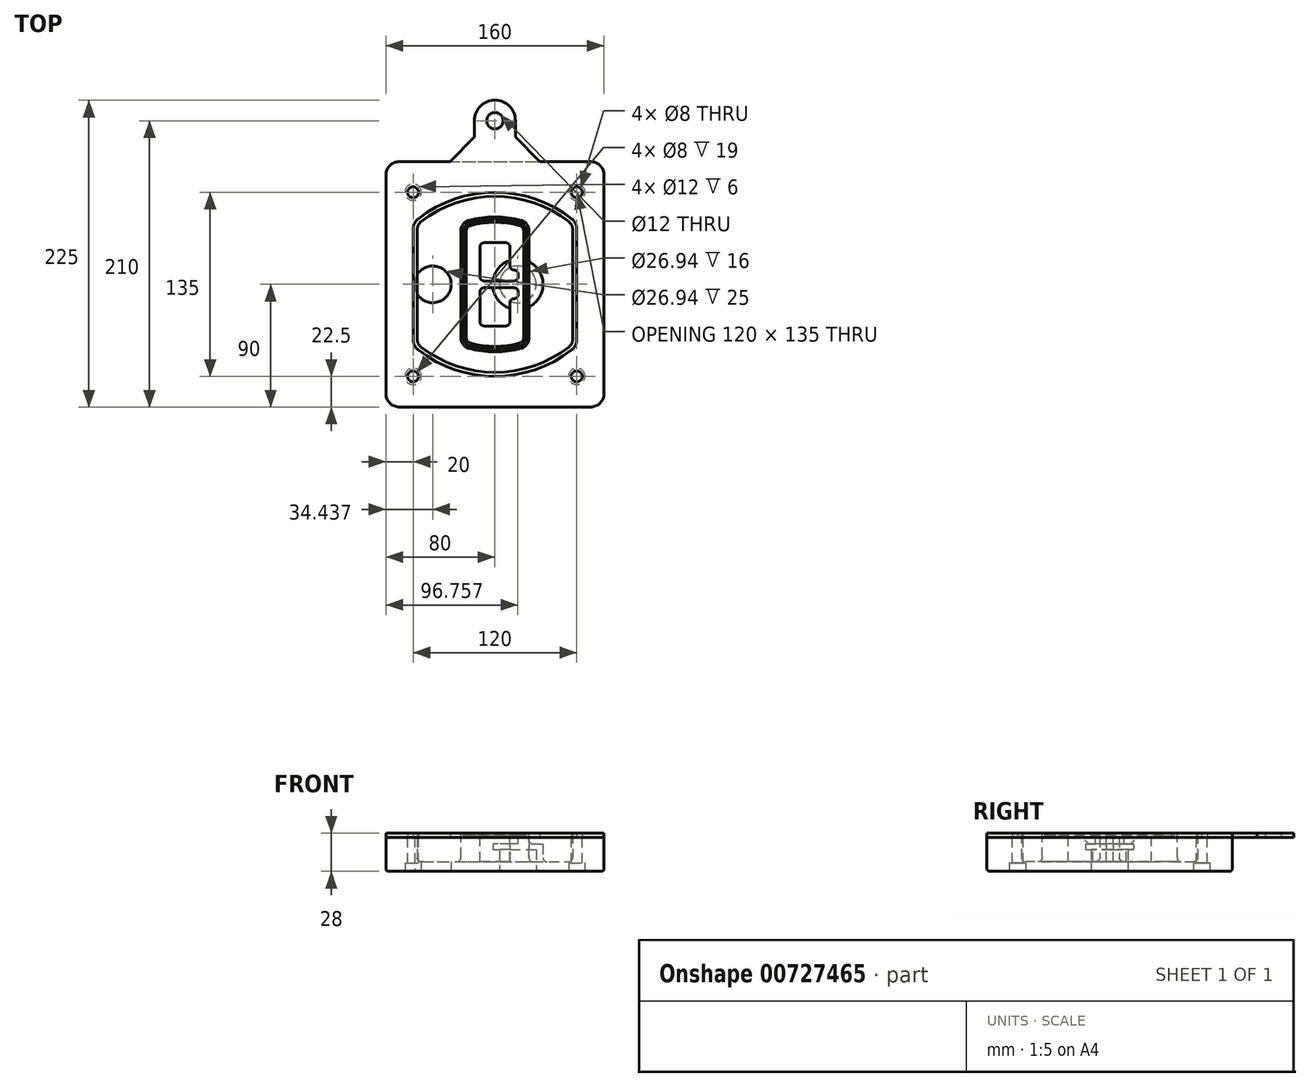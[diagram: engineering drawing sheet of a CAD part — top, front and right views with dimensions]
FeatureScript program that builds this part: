
annotation { "Feature Type Name" : "Feature", "Feature Type Description" : "" }
export const myFeature = defineFeature(function(context is Context, id is Id, definition is map)
    precondition{}
    {
        {
            var Q0;
            Q0=qCreatedBy(makeId("Top.planeOp"),FACE);
            var sketch = newSketch(context, id + "F0", { "sketchPlane" : qUnion([Q0])});
            skPoint(sketch, "E0.rect.middle", {"position": v(0, 0) * mm});
            skLineSegment(sketch, "E1.bottom", {"start": v(-70, -90) * mm, "end": v(70, -90) * mm});
            skLineSegment(sketch, "E1.top", {"start": v(-70, 90) * mm, "end": v(70, 90) * mm});
            skLineSegment(sketch, "E1.left", {"start": v(-80, -80) * mm, "end": v(-80, 80) * mm});
            skLineSegment(sketch, "E1.right", {"start": v(80, -80) * mm, "end": v(80, 80) * mm});
            skLineSegment(sketch, "E2", {"start": v(-80, 90) * mm, "end": v(80, -90) * mm, "construction": true});
            skLineSegment(sketch, "E3", {"start": v(80, 90) * mm, "end": v(-80, -90) * mm, "construction": true});
            skCircle(sketch, "E4", {"center": v(-60, 67.5) * mm, "radius": 4 * mm});
            skCircle(sketch, "E5", {"center": v(60, 67.5) * mm, "radius": 4 * mm});
            skCircle(sketch, "E6", {"center": v(60, -67.5) * mm, "radius": 4 * mm});
            skCircle(sketch, "E7", {"center": v(-60, -67.5) * mm, "radius": 4 * mm});
            skLineSegment(sketch, "E8", {"start": v(-60, 67.5) * mm, "end": v(60, 67.5) * mm, "construction": true});
            skLineSegment(sketch, "E9", {"start": v(60, 67.5) * mm, "end": v(60, -67.5) * mm, "construction": true});
            skLineSegment(sketch, "E10", {"start": v(60, -67.5) * mm, "end": v(-60, -67.5) * mm, "construction": true});
            skLineSegment(sketch, "E11", {"start": v(-60, -67.5) * mm, "end": v(-60, 67.5) * mm, "construction": true});
            skLineSegment(sketch, "E12", {"start": v(-60, 40.3) * mm, "end": v(-60, -40.3) * mm});
            skLineSegment(sketch, "E13", {"start": v(60, 40.3) * mm, "end": v(60, -40.3) * mm});
            skArc(sketch, "E14", {"start": v(56.15, 48.18) * mm, "mid": v(0, 67.5) * mm, "end": v(-56.15, 48.18) * mm});
            skArc(sketch, "E15", {"start": v(-56.15, -48.18) * mm, "mid": v(0, -67.5) * mm, "end": v(56.15, -48.18) * mm});
            skLineSegment(sketch, "E16", {"start": v(-60, 0) * mm, "end": v(60, 0) * mm, "construction": true});
            skPoint(sketch, "E17.visualSharp", {"position": v(-60, -45) * mm});
            skArc(sketch, "E17.filletArc", {"start": v(-60, -40.3) * mm, "mid": v(-58.99, -44.68) * mm, "end": v(-56.15, -48.18) * mm});
            skPoint(sketch, "E18.visualSharp", {"position": v(-60, 45) * mm});
            skArc(sketch, "E18.filletArc", {"start": v(-56.15, 48.18) * mm, "mid": v(-58.99, 44.68) * mm, "end": v(-60, 40.3) * mm});
            skPoint(sketch, "E19.visualSharp", {"position": v(60, 45) * mm});
            skArc(sketch, "E19.filletArc", {"start": v(60, 40.3) * mm, "mid": v(58.99, 44.68) * mm, "end": v(56.15, 48.18) * mm});
            skPoint(sketch, "E20.visualSharp", {"position": v(60, -45) * mm});
            skArc(sketch, "E20.filletArc", {"start": v(56.15, -48.18) * mm, "mid": v(58.99, -44.68) * mm, "end": v(60, -40.3) * mm});
            skPoint(sketch, "E21.visualSharp", {"position": v(-80, 90) * mm});
            skArc(sketch, "E21.filletArc", {"start": v(-70, 90) * mm, "mid": v(-77.07, 87.07) * mm, "end": v(-80, 80) * mm});
            skPoint(sketch, "E22.visualSharp", {"position": v(80, 90) * mm});
            skArc(sketch, "E22.filletArc", {"start": v(80, 80) * mm, "mid": v(77.07, 87.07) * mm, "end": v(70, 90) * mm});
            skPoint(sketch, "E23.visualSharp", {"position": v(80, -90) * mm});
            skArc(sketch, "E23.filletArc", {"start": v(70, -90) * mm, "mid": v(77.07, -87.07) * mm, "end": v(80, -80) * mm});
            skPoint(sketch, "E24.visualSharp", {"position": v(-80, -90) * mm});
            skArc(sketch, "E24.filletArc", {"start": v(-80, -80) * mm, "mid": v(-77.07, -87.07) * mm, "end": v(-70, -90) * mm});
            skArc(sketch, "E25.0", {"start": v(57, 40.3) * mm, "mid": v(56.3, 43.36) * mm, "end": v(54.3, 45.81) * mm});
            skLineSegment(sketch, "E25.1", {"start": v(57, 40.3) * mm, "end": v(57, -40.3) * mm});
            skArc(sketch, "E25.2", {"start": v(54.3, -45.81) * mm, "mid": v(56.3, -43.36) * mm, "end": v(57, -40.3) * mm});
            skArc(sketch, "E25.3", {"start": v(-54.3, -45.81) * mm, "mid": v(0, -64.5) * mm, "end": v(54.3, -45.81) * mm});
            skArc(sketch, "E25.4", {"start": v(-57, -40.3) * mm, "mid": v(-56.3, -43.36) * mm, "end": v(-54.3, -45.81) * mm});
            skArc(sketch, "E25.5", {"start": v(54.3, 45.81) * mm, "mid": v(0, 64.5) * mm, "end": v(-54.3, 45.81) * mm});
            skLineSegment(sketch, "E25.6", {"start": v(-57, 40.3) * mm, "end": v(-57, -40.3) * mm});
            skArc(sketch, "E25.7", {"start": v(-54.3, 45.81) * mm, "mid": v(-56.3, 43.36) * mm, "end": v(-57, 40.3) * mm});
            skArc(sketch, "E26.0", {"start": v(-58.62, 51.33) * mm, "mid": v(-62.58, 46.43) * mm, "end": v(-64, 40.3) * mm});
            skArc(sketch, "E26.1", {"start": v(58.62, 51.33) * mm, "mid": v(0, 71.5) * mm, "end": v(-58.62, 51.33) * mm});
            skArc(sketch, "E26.2", {"start": v(64, 40.3) * mm, "mid": v(62.58, 46.43) * mm, "end": v(58.62, 51.33) * mm});
            skLineSegment(sketch, "E26.3", {"start": v(64, 40.3) * mm, "end": v(64, -40.3) * mm});
            skArc(sketch, "E26.4", {"start": v(58.62, -51.33) * mm, "mid": v(62.58, -46.43) * mm, "end": v(64, -40.3) * mm});
            skLineSegment(sketch, "E26.5", {"start": v(-64, 40.3) * mm, "end": v(-64, -40.3) * mm});
            skArc(sketch, "E26.6", {"start": v(-58.62, -51.33) * mm, "mid": v(0, -71.5) * mm, "end": v(58.62, -51.33) * mm});
            skArc(sketch, "E26.7", {"start": v(-64, -40.3) * mm, "mid": v(-62.58, -46.43) * mm, "end": v(-58.62, -51.33) * mm});
            skSolve(sketch);
        }
        {
            var Q0;
            Q0=makeQuery(id+"F0.imprint","IMPRINT",FACE,{"disambiguationData":[TD([[makeQuery(id+"F0.imprint","IMPRINT",EDGE,{"derivedFrom":sQuery(id+"F0.wireOp",EDGE,"E1.bottom")}),1.0]])]});
            var Q1;
            Q1=makeQuery(id+"F0.imprint","IMPRINT",FACE,{"disambiguationData":[TD([[makeQuery(id+"F0.imprint","IMPRINT",EDGE,{"derivedFrom":sQuery(id+"F0.wireOp",EDGE,"E12")}),1.0]])]});
            var Q2;
            Q2=makeQuery(id+"F0.imprint","IMPRINT",FACE,{"disambiguationData":[TD([[makeQuery(id+"F0.imprint","IMPRINT",EDGE,{"derivedFrom":sQuery(id+"F0.wireOp",EDGE,"E25.0")}),1.0]])]});
            var Q3;
            Q3=makeQuery(id+"F0.imprint","IMPRINT",FACE,{"disambiguationData":[TD([[makeQuery(id+"F0.imprint","IMPRINT",EDGE,{"derivedFrom":sQuery(id+"F0.wireOp",EDGE,"E12")}),-1.0]])]});
            extrude(context, id + "F1", {"entities" : qUnion([Q0, Q1, Q2, Q3]), "oppositeDirection" : true, "depth" : 25 * mm});
        }
        {
            var Q0;
            Q0=makeQuery(id+"F0.imprint","IMPRINT",FACE,{"disambiguationData":[TD([[makeQuery(id+"F0.imprint","IMPRINT",EDGE,{"derivedFrom":sQuery(id+"F0.wireOp",EDGE,"E12")}),1.0]])]});
            extrude(context, id + "F2", {"entities" : qUnion([Q0]), "operationType" : NewBodyOperationType.ADD, "depth" : 3 * mm});
        }
        {
            var Q0;
            Q0=makeQuery(id+"F0.imprint","IMPRINT",FACE,{"disambiguationData":[TD([[makeQuery(id+"F0.imprint","IMPRINT",EDGE,{"derivedFrom":sQuery(id+"F0.wireOp",EDGE,"E25.0")}),1.0]])]});
            extrude(context, id + "F3", {"entities" : qUnion([Q0]), "operationType" : NewBodyOperationType.REMOVE, "oppositeDirection" : true, "depth" : 18 * mm});
        }
        {
            var Q0;
            Q0=makeQuery(id+"F2.opExtrude","CAP_FACE",FACE,{"disambiguationData":[OSD([sQuery(id+"F0.wireOp",EDGE,"E12"),sQuery(id+"F0.wireOp",EDGE,"E13"),sQuery(id+"F0.wireOp",EDGE,"E14"),sQuery(id+"F0.wireOp",EDGE,"E15"),sQuery(id+"F0.wireOp",EDGE,"E17.filletArc"),sQuery(id+"F0.wireOp",EDGE,"E18.filletArc"),sQuery(id+"F0.wireOp",EDGE,"E19.filletArc"),sQuery(id+"F0.wireOp",EDGE,"E20.filletArc"),sQuery(id+"F0.wireOp",EDGE,"E25.0"),sQuery(id+"F0.wireOp",EDGE,"E25.1"),sQuery(id+"F0.wireOp",EDGE,"E25.2"),sQuery(id+"F0.wireOp",EDGE,"E25.3"),sQuery(id+"F0.wireOp",EDGE,"E25.4"),sQuery(id+"F0.wireOp",EDGE,"E25.5"),sQuery(id+"F0.wireOp",EDGE,"E25.6"),sQuery(id+"F0.wireOp",EDGE,"E25.7")])],"isStart":false});
            var sketch = newSketch(context, id + "F4", { "sketchPlane" : qUnion([Q0])});
            skArc(sketch, "E27.0", {"start": v(-19.08, -46.97) * mm, "mid": v(0, -49.5) * mm, "end": v(19.08, -46.97) * mm});
            skArc(sketch, "E28.0", {"start": v(19.08, 46.97) * mm, "mid": v(0, 49.5) * mm, "end": v(-19.08, 46.97) * mm});
            skLineSegment(sketch, "E29", {"start": v(-25, 39.25) * mm, "end": v(-25, -39.25) * mm});
            skLineSegment(sketch, "E30", {"start": v(25, 39.25) * mm, "end": v(25, -39.25) * mm});
            skLineSegment(sketch, "E31", {"start": v(-25, 45.1) * mm, "end": v(25, 45.1) * mm, "construction": true});
            skLineSegment(sketch, "E32", {"start": v(-25, -45.1) * mm, "end": v(25, -45.1) * mm, "construction": true});
            skPoint(sketch, "E33.visualSharp", {"position": v(-25, 45.1) * mm});
            skArc(sketch, "E33.filletArc", {"start": v(-19.08, 46.97) * mm, "mid": v(-23.35, 44.11) * mm, "end": v(-25, 39.25) * mm});
            skPoint(sketch, "E34.visualSharp", {"position": v(25, 45.1) * mm});
            skArc(sketch, "E34.filletArc", {"start": v(25, 39.25) * mm, "mid": v(23.35, 44.11) * mm, "end": v(19.08, 46.97) * mm});
            skPoint(sketch, "E35.visualSharp", {"position": v(25, -45.1) * mm});
            skArc(sketch, "E35.filletArc", {"start": v(19.08, -46.97) * mm, "mid": v(23.35, -44.11) * mm, "end": v(25, -39.25) * mm});
            skPoint(sketch, "E36.visualSharp", {"position": v(-25, -45.1) * mm});
            skArc(sketch, "E36.filletArc", {"start": v(-25, -39.25) * mm, "mid": v(-23.35, -44.11) * mm, "end": v(-19.08, -46.97) * mm});
            skArc(sketch, "E37.0", {"start": v(54.3, 45.81) * mm, "mid": v(0, 64.5) * mm, "end": v(-54.3, 45.81) * mm});
            skArc(sketch, "E37.1", {"start": v(-54.3, 45.81) * mm, "mid": v(-56.3, 43.36) * mm, "end": v(-57, 40.3) * mm});
            skLineSegment(sketch, "E37.2", {"start": v(-57, 40.3) * mm, "end": v(-57, -40.3) * mm});
            skArc(sketch, "E37.3", {"start": v(-57, -40.3) * mm, "mid": v(-56.3, -43.36) * mm, "end": v(-54.3, -45.81) * mm});
            skArc(sketch, "E37.4", {"start": v(-54.3, -45.81) * mm, "mid": v(0, -64.5) * mm, "end": v(54.3, -45.81) * mm});
            skArc(sketch, "E37.5", {"start": v(54.3, -45.81) * mm, "mid": v(56.3, -43.36) * mm, "end": v(57, -40.3) * mm});
            skLineSegment(sketch, "E37.6", {"start": v(57, 40.3) * mm, "end": v(57, -40.3) * mm});
            skArc(sketch, "E37.7", {"start": v(57, 40.3) * mm, "mid": v(56.3, 43.36) * mm, "end": v(54.3, 45.81) * mm});
            skLineSegment(sketch, "E38.0", {"start": v(23, 39.25) * mm, "end": v(23, -39.25) * mm});
            skArc(sketch, "E38.1", {"start": v(18.56, -45.04) * mm, "mid": v(21.76, -42.9) * mm, "end": v(23, -39.25) * mm});
            skArc(sketch, "E38.2", {"start": v(-18.56, -45.04) * mm, "mid": v(0, -47.5) * mm, "end": v(18.56, -45.04) * mm});
            skArc(sketch, "E38.3", {"start": v(-23, -39.25) * mm, "mid": v(-21.76, -42.9) * mm, "end": v(-18.56, -45.04) * mm});
            skLineSegment(sketch, "E38.4", {"start": v(-23, 39.25) * mm, "end": v(-23, -39.25) * mm});
            skArc(sketch, "E38.5", {"start": v(23, 39.25) * mm, "mid": v(21.76, 42.9) * mm, "end": v(18.56, 45.04) * mm});
            skArc(sketch, "E38.6", {"start": v(-18.56, 45.04) * mm, "mid": v(-21.76, 42.9) * mm, "end": v(-23, 39.25) * mm});
            skArc(sketch, "E38.7", {"start": v(18.56, 45.04) * mm, "mid": v(0, 47.5) * mm, "end": v(-18.56, 45.04) * mm});
            skArc(sketch, "E39.0", {"start": v(21, 39.25) * mm, "mid": v(20.18, 41.68) * mm, "end": v(18.04, 43.1) * mm});
            skLineSegment(sketch, "E39.1", {"start": v(21, 39.25) * mm, "end": v(21, -39.25) * mm});
            skArc(sketch, "E39.2", {"start": v(18.04, -43.1) * mm, "mid": v(20.18, -41.68) * mm, "end": v(21, -39.25) * mm});
            skArc(sketch, "E39.3", {"start": v(-18.04, -43.1) * mm, "mid": v(0, -45.5) * mm, "end": v(18.04, -43.1) * mm});
            skArc(sketch, "E39.4", {"start": v(-21, -39.25) * mm, "mid": v(-20.18, -41.68) * mm, "end": v(-18.04, -43.1) * mm});
            skArc(sketch, "E39.5", {"start": v(18.04, 43.1) * mm, "mid": v(0, 45.5) * mm, "end": v(-18.04, 43.1) * mm});
            skLineSegment(sketch, "E39.6", {"start": v(-21, 39.25) * mm, "end": v(-21, -39.25) * mm});
            skArc(sketch, "E39.7", {"start": v(-18.04, 43.1) * mm, "mid": v(-20.18, 41.68) * mm, "end": v(-21, 39.25) * mm});
            skLineSegment(sketch, "E40", {"start": v(-25, 0) * mm, "end": v(25, 0) * mm, "construction": true});
            skLineSegment(sketch, "E41", {"start": v(-11, 5.5) * mm, "end": v(-11, 27.5) * mm});
            skLineSegment(sketch, "E42", {"start": v(-8, 30.5) * mm, "end": v(8, 30.5) * mm});
            skLineSegment(sketch, "E43", {"start": v(11, 27.5) * mm, "end": v(11, 13.5) * mm});
            skLineSegment(sketch, "E44", {"start": v(14, 10.5) * mm, "end": v(14, 10.5) * mm});
            skLineSegment(sketch, "E45", {"start": v(17, 7.5) * mm, "end": v(17, 5.5) * mm});
            skLineSegment(sketch, "E46", {"start": v(14, 2.5) * mm, "end": v(-8, 2.5) * mm});
            skPoint(sketch, "E47.visualSharp", {"position": v(-11, 30.5) * mm});
            skArc(sketch, "E47.filletArc", {"start": v(-8, 30.5) * mm, "mid": v(-10.12, 29.62) * mm, "end": v(-11, 27.5) * mm});
            skPoint(sketch, "E48.visualSharp", {"position": v(11, 30.5) * mm});
            skArc(sketch, "E48.filletArc", {"start": v(11, 27.5) * mm, "mid": v(10.12, 29.62) * mm, "end": v(8, 30.5) * mm});
            skPoint(sketch, "E49.visualSharp", {"position": v(11, 10.5) * mm});
            skArc(sketch, "E49.filletArc", {"start": v(11, 13.5) * mm, "mid": v(11.88, 11.38) * mm, "end": v(14, 10.5) * mm});
            skPoint(sketch, "E50.visualSharp", {"position": v(17, 10.5) * mm});
            skArc(sketch, "E50.filletArc", {"start": v(17, 7.5) * mm, "mid": v(16.12, 9.62) * mm, "end": v(14, 10.5) * mm});
            skPoint(sketch, "E51.visualSharp", {"position": v(17, 2.5) * mm});
            skArc(sketch, "E51.filletArc", {"start": v(14, 2.5) * mm, "mid": v(16.12, 3.38) * mm, "end": v(17, 5.5) * mm});
            skPoint(sketch, "E52.visualSharp", {"position": v(-11, 2.5) * mm});
            skArc(sketch, "E52.filletArc", {"start": v(-11, 5.5) * mm, "mid": v(-10.12, 3.38) * mm, "end": v(-8, 2.5) * mm});
            skLineSegment(sketch, "E53.0.MirrorCS", {"start": v(14, -2.5) * mm, "end": v(-8, -2.5) * mm});
            skArc(sketch, "E54.0.MirrorCS", {"start": v(-11, -5.5) * mm, "mid": v(-10.12, -3.38) * mm, "end": v(-8, -2.5) * mm});
            skLineSegment(sketch, "E55.0.MirrorCS", {"start": v(-11, -5.5) * mm, "end": v(-11, -27.5) * mm});
            skArc(sketch, "E56.0.MirrorCS", {"start": v(-8, -30.5) * mm, "mid": v(-10.12, -29.62) * mm, "end": v(-11, -27.5) * mm});
            skLineSegment(sketch, "E57.0.MirrorCS", {"start": v(-8, -30.5) * mm, "end": v(8, -30.5) * mm});
            skArc(sketch, "E58.0.MirrorCS", {"start": v(11, -27.5) * mm, "mid": v(10.12, -29.62) * mm, "end": v(8, -30.5) * mm});
            skLineSegment(sketch, "E59.0.MirrorCS", {"start": v(11, -27.5) * mm, "end": v(11, -13.5) * mm});
            skArc(sketch, "E60.0.MirrorCS", {"start": v(11, -13.5) * mm, "mid": v(11.88, -11.38) * mm, "end": v(14, -10.5) * mm});
            skArc(sketch, "E61.0.MirrorCS", {"start": v(17, -7.5) * mm, "mid": v(16.12, -9.62) * mm, "end": v(14, -10.5) * mm});
            skLineSegment(sketch, "E62.0.MirrorCS", {"start": v(17, -7.5) * mm, "end": v(17, -5.5) * mm});
            skArc(sketch, "E63.0.MirrorCS", {"start": v(14, -2.5) * mm, "mid": v(16.12, -3.38) * mm, "end": v(17, -5.5) * mm});
            skSolve(sketch);
        }
        {
            var Q0;
            Q0=makeQuery(id+"F4.imprint","IMPRINT",FACE,{"disambiguationData":[TD([[makeQuery(id+"F4.imprint","IMPRINT",EDGE,{"derivedFrom":sQuery(id+"F4.wireOp",EDGE,"E27.0")}),1.0]])]});
            var Q1;
            Q1=makeQuery(id+"F4.imprint","IMPRINT",FACE,{"disambiguationData":[TD([[makeQuery(id+"F4.imprint","IMPRINT",EDGE,{"derivedFrom":sQuery(id+"F4.wireOp",EDGE,"E38.0")}),-1.0]])]});
            var Q2;
            Q2=makeQuery(id+"F4.imprint","IMPRINT",FACE,{"disambiguationData":[TD([[makeQuery(id+"F4.imprint","IMPRINT",EDGE,{"derivedFrom":sQuery(id+"F4.wireOp",EDGE,"E39.0")}),1.0]])]});
            extrude(context, id + "F5", {"entities" : qUnion([Q0, Q1, Q2]), "operationType" : NewBodyOperationType.ADD, "endBound" : BoundingType.UP_TO_NEXT, "oppositeDirection" : true, "depth" : 25 * mm});
        }
        {
            var Q0;
            Q0=makeQuery(id+"F4.imprint","IMPRINT",FACE,{"disambiguationData":[TD([[makeQuery(id+"F4.imprint","IMPRINT",EDGE,{"derivedFrom":sQuery(id+"F4.wireOp",EDGE,"E38.0")}),-1.0]])]});
            extrude(context, id + "F6", {"entities" : qUnion([Q0]), "operationType" : NewBodyOperationType.REMOVE, "oppositeDirection" : true, "depth" : 2 * mm});
        }
        {
            var Q0;
            Q0=makeQuery(id+"F1.opExtrude","CAP_FACE",FACE,{"disambiguationData":[OSD([sQuery(id+"F0.wireOp",EDGE,"E1.bottom"),sQuery(id+"F0.wireOp",EDGE,"E1.top"),sQuery(id+"F0.wireOp",EDGE,"E1.left"),sQuery(id+"F0.wireOp",EDGE,"E1.right"),sQuery(id+"F0.wireOp",EDGE,"E4"),sQuery(id+"F0.wireOp",EDGE,"E5"),sQuery(id+"F0.wireOp",EDGE,"E6"),sQuery(id+"F0.wireOp",EDGE,"E7"),sQuery(id+"F0.wireOp",EDGE,"E21.filletArc"),sQuery(id+"F0.wireOp",EDGE,"E22.filletArc"),sQuery(id+"F0.wireOp",EDGE,"E23.filletArc"),sQuery(id+"F0.wireOp",EDGE,"E24.filletArc")])],"isStart":false});
            var sketch = newSketch(context, id + "F7", { "sketchPlane" : qUnion([Q0])});
            skCircle(sketch, "E64", {"center": v(16.76, 0) * mm, "radius": 13.47 * mm});
            skCircle(sketch, "E65", {"center": v(-45.56, 0) * mm, "radius": 13.47 * mm});
            skLineSegment(sketch, "E66", {"start": v(80, 0) * mm, "end": v(-80, 0) * mm});
            skCircle(sketch, "E67", {"center": v(16.76, 0) * mm, "radius": 18.47 * mm});
            skCircle(sketch, "E68", {"center": v(60, -67.5) * mm, "radius": 6 * mm});
            skCircle(sketch, "E69", {"center": v(-60, -67.5) * mm, "radius": 6 * mm});
            skCircle(sketch, "E70", {"center": v(-60, 67.5) * mm, "radius": 6 * mm});
            skCircle(sketch, "E71", {"center": v(60, 67.5) * mm, "radius": 6 * mm});
            skSolve(sketch);
        }
        {
            var Q0;
            {var subQ1=sQuery(id+"F7.wireOp",EDGE,"E66");var subQ4=sQuery(id+"F7.wireOp",EDGE,"E64");var subQ6=makeQuery(id+"F7.imprint","INTERSECT",VERTEX,{"disambiguationData":[OD(0.0)],"derivedFrom":[subQ4,subQ1]});Q0=makeQuery(id+"F7.imprint","IMPRINT",FACE,{"disambiguationData":[TD([[makeQuery(id+"F7.imprint","IMPRINT",EDGE,{"disambiguationData":[TD([[subQ6,-1.0]])],"derivedFrom":subQ4}),-1.0]])]});}
            var Q1;
            {var subQ0=sQuery(id+"F7.wireOp",EDGE,"E66");var subQ1=sQuery(id+"F7.wireOp",EDGE,"E64");var subQ3=makeQuery(id+"F7.imprint","INTERSECT",VERTEX,{"disambiguationData":[OD(0.0)],"derivedFrom":[subQ1,subQ0]});Q1=makeQuery(id+"F7.imprint","IMPRINT",FACE,{"disambiguationData":[TD([[makeQuery(id+"F7.imprint","IMPRINT",EDGE,{"disambiguationData":[TD([[subQ3,-1.0]])],"derivedFrom":subQ1}),1.0]])]});}
            var Q2;
            {var subQ0=sQuery(id+"F7.wireOp",EDGE,"E66");var subQ1=sQuery(id+"F7.wireOp",EDGE,"E64");var subQ3=makeQuery(id+"F7.imprint","INTERSECT",VERTEX,{"disambiguationData":[OD(0.0)],"derivedFrom":[subQ1,subQ0]});Q2=makeQuery(id+"F7.imprint","IMPRINT",FACE,{"disambiguationData":[TD([[makeQuery(id+"F7.imprint","IMPRINT",EDGE,{"disambiguationData":[TD([[subQ3,1.0]])],"derivedFrom":subQ1}),1.0]])]});}
            var Q3;
            {var subQ1=sQuery(id+"F7.wireOp",EDGE,"E66");var subQ4=sQuery(id+"F7.wireOp",EDGE,"E64");var subQ6=makeQuery(id+"F7.imprint","INTERSECT",VERTEX,{"disambiguationData":[OD(0.0)],"derivedFrom":[subQ4,subQ1]});Q3=makeQuery(id+"F7.imprint","IMPRINT",FACE,{"disambiguationData":[TD([[makeQuery(id+"F7.imprint","IMPRINT",EDGE,{"disambiguationData":[TD([[subQ6,1.0]])],"derivedFrom":subQ4}),-1.0]])]});}
            extrude(context, id + "F8", {"entities" : qUnion([Q0, Q1, Q2, Q3]), "operationType" : NewBodyOperationType.ADD, "oppositeDirection" : true, "depth" : 20 * mm});
        }
        {
            var Q0;
            {var subQ0=sQuery(id+"F7.wireOp",EDGE,"E66");var subQ1=sQuery(id+"F7.wireOp",EDGE,"E64");var subQ3=makeQuery(id+"F7.imprint","INTERSECT",VERTEX,{"disambiguationData":[OD(0.0)],"derivedFrom":[subQ1,subQ0]});Q0=makeQuery(id+"F7.imprint","IMPRINT",FACE,{"disambiguationData":[TD([[makeQuery(id+"F7.imprint","IMPRINT",EDGE,{"disambiguationData":[TD([[subQ3,-1.0]])],"derivedFrom":subQ1}),1.0]])]});}
            var Q1;
            {var subQ0=sQuery(id+"F7.wireOp",EDGE,"E66");var subQ1=sQuery(id+"F7.wireOp",EDGE,"E64");var subQ3=makeQuery(id+"F7.imprint","INTERSECT",VERTEX,{"disambiguationData":[OD(0.0)],"derivedFrom":[subQ1,subQ0]});Q1=makeQuery(id+"F7.imprint","IMPRINT",FACE,{"disambiguationData":[TD([[makeQuery(id+"F7.imprint","IMPRINT",EDGE,{"disambiguationData":[TD([[subQ3,1.0]])],"derivedFrom":subQ1}),1.0]])]});}
            extrude(context, id + "F9", {"entities" : qUnion([Q0, Q1]), "operationType" : NewBodyOperationType.REMOVE, "oppositeDirection" : true, "depth" : 16 * mm});
        }
        {
            var Q0;
            {var subQ0=sQuery(id+"F7.wireOp",EDGE,"E66");var subQ1=sQuery(id+"F7.wireOp",EDGE,"E65");var subQ3=makeQuery(id+"F7.imprint","INTERSECT",VERTEX,{"disambiguationData":[OD(0.0)],"derivedFrom":[subQ1,subQ0]});Q0=makeQuery(id+"F7.imprint","IMPRINT",FACE,{"disambiguationData":[TD([[makeQuery(id+"F7.imprint","IMPRINT",EDGE,{"disambiguationData":[TD([[subQ3,-1.0]])],"derivedFrom":subQ1}),1.0]])]});}
            var Q1;
            {var subQ0=sQuery(id+"F7.wireOp",EDGE,"E66");var subQ1=sQuery(id+"F7.wireOp",EDGE,"E65");var subQ3=makeQuery(id+"F7.imprint","INTERSECT",VERTEX,{"disambiguationData":[OD(0.0)],"derivedFrom":[subQ1,subQ0]});Q1=makeQuery(id+"F7.imprint","IMPRINT",FACE,{"disambiguationData":[TD([[makeQuery(id+"F7.imprint","IMPRINT",EDGE,{"disambiguationData":[TD([[subQ3,1.0]])],"derivedFrom":subQ1}),1.0]])]});}
            extrude(context, id + "F10", {"entities" : qUnion([Q0, Q1]), "operationType" : NewBodyOperationType.REMOVE, "oppositeDirection" : true, "depth" : 25 * mm});
        }
        {
            var Q0;
            Q0=makeQuery(id+"F7.imprint","IMPRINT",FACE,{"disambiguationData":[TD([[makeQuery(id+"F7.imprint","IMPRINT",EDGE,{"derivedFrom":sQuery(id+"F7.wireOp",EDGE,"E68")}),1.0]])]});
            var Q1;
            Q1=makeQuery(id+"F7.imprint","IMPRINT",FACE,{"disambiguationData":[TD([[makeQuery(id+"F7.imprint","IMPRINT",EDGE,{"derivedFrom":makeQuery(id+"F1.opExtrude","CAP_EDGE",EDGE,{"disambiguationData":[OSD([sQuery(id+"F0.wireOp",EDGE,"E5")])],"isStart":false})}),-1.0]])]});
            var Q2;
            Q2=makeQuery(id+"F7.imprint","IMPRINT",FACE,{"disambiguationData":[TD([[makeQuery(id+"F7.imprint","IMPRINT",EDGE,{"derivedFrom":sQuery(id+"F7.wireOp",EDGE,"E69")}),1.0]])]});
            var Q3;
            Q3=makeQuery(id+"F7.imprint","IMPRINT",FACE,{"disambiguationData":[TD([[makeQuery(id+"F7.imprint","IMPRINT",EDGE,{"derivedFrom":makeQuery(id+"F1.opExtrude","CAP_EDGE",EDGE,{"disambiguationData":[OSD([sQuery(id+"F0.wireOp",EDGE,"E4")])],"isStart":false})}),-1.0]])]});
            var Q4;
            Q4=makeQuery(id+"F7.imprint","IMPRINT",FACE,{"disambiguationData":[TD([[makeQuery(id+"F7.imprint","IMPRINT",EDGE,{"derivedFrom":sQuery(id+"F7.wireOp",EDGE,"E70")}),1.0]])]});
            var Q5;
            Q5=makeQuery(id+"F7.imprint","IMPRINT",FACE,{"disambiguationData":[TD([[makeQuery(id+"F7.imprint","IMPRINT",EDGE,{"derivedFrom":makeQuery(id+"F1.opExtrude","CAP_EDGE",EDGE,{"disambiguationData":[OSD([sQuery(id+"F0.wireOp",EDGE,"E7")])],"isStart":false})}),-1.0]])]});
            var Q6;
            Q6=makeQuery(id+"F7.imprint","IMPRINT",FACE,{"disambiguationData":[TD([[makeQuery(id+"F7.imprint","IMPRINT",EDGE,{"derivedFrom":sQuery(id+"F7.wireOp",EDGE,"E71")}),1.0]])]});
            var Q7;
            Q7=makeQuery(id+"F7.imprint","IMPRINT",FACE,{"disambiguationData":[TD([[makeQuery(id+"F7.imprint","IMPRINT",EDGE,{"derivedFrom":makeQuery(id+"F1.opExtrude","CAP_EDGE",EDGE,{"disambiguationData":[OSD([sQuery(id+"F0.wireOp",EDGE,"E6")])],"isStart":false})}),-1.0]])]});
            extrude(context, id + "F11", {"entities" : qUnion([Q0, Q1, Q2, Q3, Q4, Q5, Q6, Q7]), "operationType" : NewBodyOperationType.REMOVE, "oppositeDirection" : true, "depth" : 6 * mm});
        }
        {
            var Q0;
            Q0=makeQuery(id+"F9.boolean.opBoolean","COPY",FACE,{"derivedFrom":makeQuery(id+"F9.opExtrude","CAP_FACE",FACE,{"disambiguationData":[OSD([sQuery(id+"F7.wireOp",EDGE,"E64")])],"isStart":false})});
            var sketch = newSketch(context, id + "F12", { "sketchPlane" : qUnion([Q0])});
            skArc(sketch, "E72.0", {"start": v(11, 17.55) * mm, "mid": v(2.57, 11.82) * mm, "end": v(-1.54, 2.5) * mm});
            skArc(sketch, "E72.1", {"start": v(-1.54, -2.5) * mm, "mid": v(2.57, -11.82) * mm, "end": v(11, -17.55) * mm});
            skLineSegment(sketch, "E73", {"start": v(-1.54, -2.5) * mm, "end": v(14, -2.5) * mm});
            skLineSegment(sketch, "E74.0", {"start": v(14, 2.5) * mm, "end": v(-1.54, 2.5) * mm});
            skArc(sketch, "E74.1", {"start": v(14, 2.5) * mm, "mid": v(16.12, 3.38) * mm, "end": v(17, 5.5) * mm});
            skLineSegment(sketch, "E74.2", {"start": v(17, 7.5) * mm, "end": v(17, 5.5) * mm});
            skArc(sketch, "E74.3", {"start": v(17, 7.5) * mm, "mid": v(16.12, 9.62) * mm, "end": v(14, 10.5) * mm});
            skArc(sketch, "E74.4", {"start": v(11, 13.5) * mm, "mid": v(11.88, 11.38) * mm, "end": v(14, 10.5) * mm});
            skLineSegment(sketch, "E74.5", {"start": v(11, 17.55) * mm, "end": v(11, 13.5) * mm});
            skLineSegment(sketch, "E74.7", {"start": v(14, -2.5) * mm, "end": v(-1.54, -2.5) * mm});
            skArc(sketch, "E74.8", {"start": v(14, -2.5) * mm, "mid": v(16.12, -3.38) * mm, "end": v(17, -5.5) * mm});
            skLineSegment(sketch, "E74.9", {"start": v(17, -7.5) * mm, "end": v(17, -5.5) * mm});
            skArc(sketch, "E74.10", {"start": v(17, -7.5) * mm, "mid": v(16.12, -9.62) * mm, "end": v(14, -10.5) * mm});
            skArc(sketch, "E74.11", {"start": v(11, -13.5) * mm, "mid": v(11.88, -11.38) * mm, "end": v(14, -10.5) * mm});
            skLineSegment(sketch, "E74.12", {"start": v(11, -17.55) * mm, "end": v(11, -13.5) * mm});
            skPoint(sketch, "E75.orphan", {"position": v(11, -27.5) * mm});
            skPoint(sketch, "E76.orphan", {"position": v(-8, -2.5) * mm});
            skPoint(sketch, "E77.orphan", {"position": v(-8, 2.5) * mm});
            skPoint(sketch, "E78.orphan", {"position": v(11, 27.5) * mm});
            skSolve(sketch);
        }
        {
            var Q0;
            {var subQ7=sQuery(id+"F12.wireOp",EDGE,"E72.0");var subQ14=sQuery(id+"F12.wireOp",EDGE,"E72.1");var subQ16=sQuery(id+"F12.wireOp",EDGE,"E74.1");var subQ18=sQuery(id+"F12.wireOp",EDGE,"E74.8");Q0=qUnion([makeQuery(id+"F12.imprint","IMPRINT",FACE,{"disambiguationData":[TD([[makeQuery(id+"F12.imprint","IMPRINT",EDGE,{"derivedFrom":subQ7}),1.0]])]}),makeQuery(id+"F12.imprint","IMPRINT",FACE,{"disambiguationData":[TD([[makeQuery(id+"F12.imprint","IMPRINT",EDGE,{"derivedFrom":subQ14}),1.0]])]}),makeQuery(id+"F12.imprint","IMPRINT",FACE,{"disambiguationData":[TD([[makeQuery(id+"F12.imprint","IMPRINT",EDGE,{"derivedFrom":subQ16}),1.0]])]}),makeQuery(id+"F12.imprint","IMPRINT",FACE,{"disambiguationData":[TD([[makeQuery(id+"F12.imprint","IMPRINT",EDGE,{"derivedFrom":subQ18}),-1.0]])]})]);}
            var Q1;
            Q1=makeQuery(id+"F5.boolean.opBoolean","SPLIT",FACE,{"disambiguationData":[TD([makeQuery(id+"F5.opExtrude","SWEPT_FACE",FACE,{"disambiguationData":[OSD([sQuery(id+"F4.wireOp",EDGE,"E41")])]})])],"derivedFrom":makeQuery(id+"F3.boolean.opBoolean","COPY",FACE,{"derivedFrom":makeQuery(id+"F3.opExtrude","CAP_FACE",FACE,{"disambiguationData":[OSD([sQuery(id+"F0.wireOp",EDGE,"E25.0"),sQuery(id+"F0.wireOp",EDGE,"E25.1"),sQuery(id+"F0.wireOp",EDGE,"E25.2"),sQuery(id+"F0.wireOp",EDGE,"E25.3"),sQuery(id+"F0.wireOp",EDGE,"E25.4"),sQuery(id+"F0.wireOp",EDGE,"E25.5"),sQuery(id+"F0.wireOp",EDGE,"E25.6"),sQuery(id+"F0.wireOp",EDGE,"E25.7")])],"isStart":false})})});
            extrude(context, id + "F13", {"entities" : qUnion([Q0]), "operationType" : NewBodyOperationType.REMOVE, "endBound" : BoundingType.UP_TO_SURFACE, "endBoundEntityFace" : qUnion([Q1]), "depth" : 25 * mm});
        }
        {
            var Q0;
            Q0=makeQuery(id+"F3.boolean.opBoolean","COPY",EDGE,{"derivedFrom":makeQuery(id+"F3.opExtrude","CAP_EDGE",EDGE,{"disambiguationData":[OSD([sQuery(id+"F0.wireOp",EDGE,"E25.6")])],"isStart":false})});
            var Q1;
            Q1=makeQuery(id+"F8.boolean.opBoolean","INTERSECT",EDGE,{"derivedFrom":[makeQuery(id+"F5.opExtrude","SWEPT_FACE",FACE,{"disambiguationData":[OSD([sQuery(id+"F4.wireOp",EDGE,"E30")])]}),makeQuery(id+"F8.opExtrude","CAP_FACE",FACE,{"disambiguationData":[OSD([sQuery(id+"F7.wireOp",EDGE,"E67")])],"isStart":false})]});
            var Q2;
            Q2=makeQuery(id+"F8.boolean.opBoolean","INTERSECT",EDGE,{"disambiguationData":[OD(1.0)],"derivedFrom":[makeQuery(id+"F5.opExtrude","SWEPT_FACE",FACE,{"disambiguationData":[OSD([sQuery(id+"F4.wireOp",EDGE,"E30")])]}),makeQuery(id+"F8.opExtrude","SWEPT_FACE",FACE,{"disambiguationData":[OSD([sQuery(id+"F7.wireOp",EDGE,"E67")])]})]});
            var Q3;
            {var subQ0=sQuery(id+"F4.wireOp",EDGE,"E30");Q3=makeQuery(id+"F8.boolean.opBoolean","SPLIT",EDGE,{"disambiguationData":[TD([makeQuery(id+"F5.opExtrude","SWEPT_FACE",FACE,{"disambiguationData":[OSD([sQuery(id+"F4.wireOp",EDGE,"E35.filletArc")])]})])],"derivedFrom":makeQuery(id+"F5.opExtrude","CAP_EDGE",EDGE,{"disambiguationData":[OSD([subQ0])],"isStart":false})});}
            var Q4;
            {var subQ0=sQuery(id+"F0.wireOp",EDGE,"E25.7");var subQ1=sQuery(id+"F0.wireOp",EDGE,"E25.1");var subQ2=sQuery(id+"F0.wireOp",EDGE,"E25.6");var subQ3=sQuery(id+"F0.wireOp",EDGE,"E25.5");var subQ4=sQuery(id+"F0.wireOp",EDGE,"E25.4");var subQ5=sQuery(id+"F0.wireOp",EDGE,"E25.0");var subQ6=sQuery(id+"F0.wireOp",EDGE,"E25.2");var subQ7=sQuery(id+"F0.wireOp",EDGE,"E25.3");Q4=makeQuery(id+"F8.boolean.opBoolean","INTERSECT",EDGE,{"derivedFrom":[makeQuery(id+"F5.boolean.opBoolean","SPLIT",FACE,{"disambiguationData":[TD([makeQuery(id+"F2.opExtrude","SWEPT_FACE",FACE,{"disambiguationData":[OSD([subQ5])]})])],"derivedFrom":makeQuery(id+"F3.boolean.opBoolean","COPY",FACE,{"derivedFrom":makeQuery(id+"F3.opExtrude","CAP_FACE",FACE,{"disambiguationData":[OSD([subQ5,subQ1,subQ6,subQ7,subQ4,subQ3,subQ2,subQ0])],"isStart":false})})}),makeQuery(id+"F8.opExtrude","SWEPT_FACE",FACE,{"disambiguationData":[OSD([sQuery(id+"F7.wireOp",EDGE,"E67")])]})]});}
            var Q5;
            Q5=makeQuery(id+"F8.boolean.opBoolean","INTERSECT",EDGE,{"disambiguationData":[OD(0.0)],"derivedFrom":[makeQuery(id+"F5.opExtrude","SWEPT_FACE",FACE,{"disambiguationData":[OSD([sQuery(id+"F4.wireOp",EDGE,"E30")])]}),makeQuery(id+"F8.opExtrude","SWEPT_FACE",FACE,{"disambiguationData":[OSD([sQuery(id+"F7.wireOp",EDGE,"E67")])]})]});
            fillet(context, id + "F14", {"entities" : qUnion([Q0, Q1, Q2, Q3, Q4, Q5]), "radius" : 3 * mm, "tangentPropagation" : true, "allowEdgeOverflow" : false});
        }
        {
            var Q0;
            Q0=makeQuery(id+"F1.opExtrude","CAP_EDGE",EDGE,{"disambiguationData":[OSD([sQuery(id+"F0.wireOp",EDGE,"E1.bottom")])],"isStart":false});
            fillet(context, id + "F15", {"entities" : qUnion([Q0]), "radius" : 2 * mm, "tangentPropagation" : true, "allowEdgeOverflow" : false});
        }
        {
            var Q0;
            {var subQ0=sQuery(id+"F0.wireOp",EDGE,"E21.filletArc");var subQ1=sQuery(id+"F0.wireOp",EDGE,"E7");var subQ2=sQuery(id+"F0.wireOp",EDGE,"E6");var subQ3=sQuery(id+"F0.wireOp",EDGE,"E5");var subQ4=sQuery(id+"F0.wireOp",EDGE,"E4");var subQ5=sQuery(id+"F0.wireOp",EDGE,"E22.filletArc");var subQ6=sQuery(id+"F0.wireOp",EDGE,"E1.bottom");var subQ7=sQuery(id+"F0.wireOp",EDGE,"E1.right");var subQ8=sQuery(id+"F0.wireOp",EDGE,"E1.top");var subQ9=sQuery(id+"F0.wireOp",EDGE,"E1.left");var subQ10=sQuery(id+"F0.wireOp",EDGE,"E23.filletArc");var subQ11=sQuery(id+"F0.wireOp",EDGE,"E24.filletArc");Q0=makeQuery(id+"F2.boolean.opBoolean","SPLIT",FACE,{"disambiguationData":[TD([makeQuery(id+"F1.opExtrude","SWEPT_FACE",FACE,{"disambiguationData":[OSD([subQ6])]})])],"derivedFrom":makeQuery(id+"F1.opExtrude","CAP_FACE",FACE,{"disambiguationData":[OSD([subQ6,subQ8,subQ9,subQ7,subQ4,subQ3,subQ2,subQ1,subQ0,subQ5,subQ10,subQ11])],"isStart":true})});}
            var sketch = newSketch(context, id + "F16", { "sketchPlane" : qUnion([Q0])});
            skLineSegment(sketch, "E79", {"start": v(0, 90) * mm, "end": v(0, 120) * mm, "construction": true});
            skCircle(sketch, "E80", {"center": v(0, 120) * mm, "radius": 6 * mm});
            skLineSegment(sketch, "E81", {"start": v(-33, 90) * mm, "end": v(-15, 108) * mm});
            skLineSegment(sketch, "E82", {"start": v(-15, 108) * mm, "end": v(-15, 120) * mm});
            skLineSegment(sketch, "E83", {"start": v(33, 90) * mm, "end": v(15, 108) * mm});
            skLineSegment(sketch, "E84", {"start": v(15, 108) * mm, "end": v(15, 120) * mm});
            skArc(sketch, "E85", {"start": v(15, 120) * mm, "mid": v(0, 135) * mm, "end": v(-15, 120) * mm});
            skLineSegment(sketch, "E86", {"start": v(80, 0) * mm, "end": v(-80, 0) * mm, "construction": true});
            skArc(sketch, "E87.MirrorCS", {"start": v(15, -120) * mm, "mid": v(0, -135) * mm, "end": v(-15, -120) * mm});
            skCircle(sketch, "E88.MirrorC", {"center": v(0, -120) * mm, "radius": 6 * mm});
            skLineSegment(sketch, "E89.MirrorCS", {"start": v(0, -90) * mm, "end": v(0, -120) * mm, "construction": true});
            skLineSegment(sketch, "E90.MirrorCS", {"start": v(-33, -90) * mm, "end": v(-15, -108) * mm});
            skLineSegment(sketch, "E91.MirrorCS", {"start": v(-15, -108) * mm, "end": v(-15, -120) * mm});
            skLineSegment(sketch, "E92.MirrorCS", {"start": v(33, -90) * mm, "end": v(15, -108) * mm});
            skLineSegment(sketch, "E93.MirrorCS", {"start": v(15, -108) * mm, "end": v(15, -120) * mm});
            skSolve(sketch);
        }
        {
            var Q0;
            Q0=makeQuery(id+"F16.imprint","IMPRINT",FACE,{"disambiguationData":[TD([[makeQuery(id+"F16.imprint","IMPRINT",EDGE,{"derivedFrom":sQuery(id+"F16.wireOp",EDGE,"E80")}),-1.0]])]});
            var Q1;
            Q1=makeQuery(id+"F16.imprint","IMPRINT",FACE,{"disambiguationData":[TD([[makeQuery(id+"F16.imprint","IMPRINT",EDGE,{"derivedFrom":makeQuery(id+"F1.opExtrude","CAP_EDGE",EDGE,{"disambiguationData":[OSD([sQuery(id+"F0.wireOp",EDGE,"E1.left")])],"isStart":true})}),-1.0]])]});
            var Q2;
            Q2=makeQuery(id+"F16.imprint","IMPRINT",FACE,{"disambiguationData":[TD([[makeQuery(id+"F16.imprint","IMPRINT",EDGE,{"derivedFrom":sQuery(id+"F16.wireOp",EDGE,"E87.MirrorCS")}),-1.0]])]});
            var Q3;
            Q3=makeQuery(id+"F2.opExtrude","CAP_FACE",FACE,{"disambiguationData":[OSD([sQuery(id+"F0.wireOp",EDGE,"E12"),sQuery(id+"F0.wireOp",EDGE,"E13"),sQuery(id+"F0.wireOp",EDGE,"E14"),sQuery(id+"F0.wireOp",EDGE,"E15"),sQuery(id+"F0.wireOp",EDGE,"E17.filletArc"),sQuery(id+"F0.wireOp",EDGE,"E18.filletArc"),sQuery(id+"F0.wireOp",EDGE,"E19.filletArc"),sQuery(id+"F0.wireOp",EDGE,"E20.filletArc"),sQuery(id+"F0.wireOp",EDGE,"E25.0"),sQuery(id+"F0.wireOp",EDGE,"E25.1"),sQuery(id+"F0.wireOp",EDGE,"E25.2"),sQuery(id+"F0.wireOp",EDGE,"E25.3"),sQuery(id+"F0.wireOp",EDGE,"E25.4"),sQuery(id+"F0.wireOp",EDGE,"E25.5"),sQuery(id+"F0.wireOp",EDGE,"E25.6"),sQuery(id+"F0.wireOp",EDGE,"E25.7")])],"isStart":false});
            extrude(context, id + "F17", {"entities" : qUnion([Q0, Q1, Q2]), "endBound" : BoundingType.UP_TO_SURFACE, "depth" : 25 * mm, "endBoundEntityFace" : qUnion([Q3]), "offsetDistance" : 25 * mm});
        }
    });
